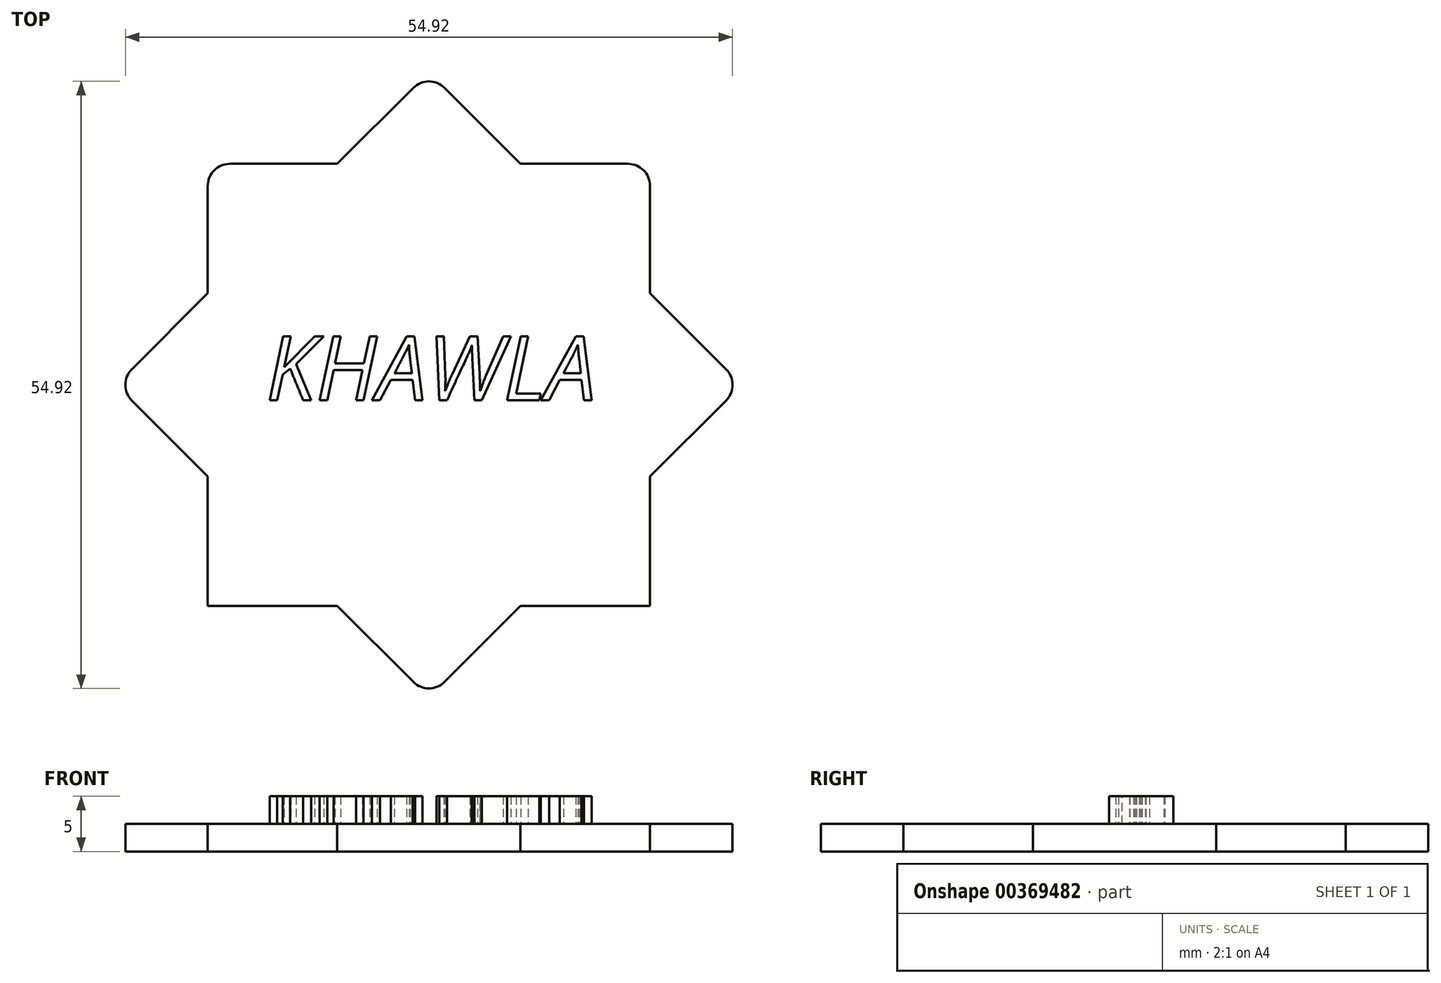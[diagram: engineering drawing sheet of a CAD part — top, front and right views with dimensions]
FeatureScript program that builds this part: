
annotation { "Feature Type Name" : "Feature", "Feature Type Description" : "" }
export const myFeature = defineFeature(function(context is Context, id is Id, definition is map)
    precondition{}
    {
        {
            var Q0;
            Q0=qCreatedBy(makeId("Top.planeOp"),FACE);
            var sketch = newSketch(context, id + "F0", { "sketchPlane" : qUnion([Q0])});
            skLineSegment(sketch, "E0.bottom", {"start": v(20, -20) * mm, "end": v(-20, -20) * mm});
            skLineSegment(sketch, "E0.top", {"start": v(18, 20) * mm, "end": v(-18, 20) * mm});
            skLineSegment(sketch, "E0.left", {"start": v(20, -20) * mm, "end": v(20, 18) * mm});
            skLineSegment(sketch, "E0.right", {"start": v(-20, -20) * mm, "end": v(-20, 18) * mm});
            skPoint(sketch, "E0.middle", {"position": v(0, 0) * mm});
            skCircle(sketch, "E1.cCircle", {"center": v(0, 0) * mm, "radius": 28.28 * mm, "construction": true});
            skLineSegment(sketch, "E1.0", {"start": v(26.87, -1.41) * mm, "end": v(1.41, -26.87) * mm});
            skLineSegment(sketch, "E1.1", {"start": v(-1.41, -26.87) * mm, "end": v(-26.87, -1.41) * mm});
            skLineSegment(sketch, "E1.2", {"start": v(-26.87, 1.41) * mm, "end": v(-1.41, 26.87) * mm});
            skLineSegment(sketch, "E1.3", {"start": v(1.41, 26.87) * mm, "end": v(26.87, 1.41) * mm});
            skPoint(sketch, "E2.visualSharp", {"position": v(0, 28.28) * mm});
            skArc(sketch, "E2.filletArc", {"start": v(1.41, 26.87) * mm, "mid": v(0, 27.46) * mm, "end": v(-1.41, 26.87) * mm});
            skPoint(sketch, "E3.visualSharp", {"position": v(28.28, 0) * mm});
            skArc(sketch, "E3.filletArc", {"start": v(26.87, -1.41) * mm, "mid": v(27.46, 0) * mm, "end": v(26.87, 1.41) * mm});
            skPoint(sketch, "E4.visualSharp", {"position": v(20, 20) * mm});
            skArc(sketch, "E4.filletArc", {"start": v(20, 18) * mm, "mid": v(19.41, 19.41) * mm, "end": v(18, 20) * mm});
            skPoint(sketch, "E5.visualSharp", {"position": v(-20, 20) * mm});
            skArc(sketch, "E5.filletArc", {"start": v(-18, 20) * mm, "mid": v(-19.41, 19.41) * mm, "end": v(-20, 18) * mm});
            skPoint(sketch, "E6.visualSharp", {"position": v(-28.28, 0) * mm});
            skArc(sketch, "E6.filletArc", {"start": v(-26.87, 1.41) * mm, "mid": v(-27.46, 0) * mm, "end": v(-26.87, -1.41) * mm});
            skPoint(sketch, "E7.visualSharp", {"position": v(0, -28.28) * mm});
            skArc(sketch, "E7.filletArc", {"start": v(-1.41, -26.87) * mm, "mid": v(0, -27.46) * mm, "end": v(1.41, -26.87) * mm});
            skSolve(sketch);
        }
        {
            var Q0;
            Q0 = qSketchRegion(id + "F0", true);
            extrude(context, id + "F1", {"entities" : qUnion([Q0]), "depth" : 2.5 * mm});
        }
        {
            var Q0;
            Q0=makeQuery(id+"F1.opExtrude","CAP_FACE",FACE,{"disambiguationData":[OSD([sQuery(id+"F0.wireOp",EDGE,"E0.bottom"),sQuery(id+"F0.wireOp",EDGE,"E0.top"),sQuery(id+"F0.wireOp",EDGE,"E0.left"),sQuery(id+"F0.wireOp",EDGE,"E0.right"),sQuery(id+"F0.wireOp",EDGE,"E1.0"),sQuery(id+"F0.wireOp",EDGE,"E1.1"),sQuery(id+"F0.wireOp",EDGE,"E1.2"),sQuery(id+"F0.wireOp",EDGE,"E1.3")])],"isStart":false});
            var sketch = newSketch(context, id + "F2", { "sketchPlane" : qUnion([Q0])});
            skSolve(sketch);
        }
        {
            var Q0;
            {var subQ3=sQuery(id+"F0.wireOp",EDGE,"E0.bottom");var subQ7=sQuery(id+"F0.wireOp",EDGE,"E0.left");var subQ18=makeQuery(id+"F0.imprint","INTERSECT",VERTEX,{"derivedFrom":[subQ3,subQ7]});Q0=makeQuery(id+"F2.imprint","IMPRINT",FACE,{"disambiguationData":[TD([[makeQuery(id+"F2.imprint","IMPRINT",EDGE,{"derivedFrom":makeQuery(id+"F1.opExtrude","CAP_EDGE",EDGE,{"disambiguationData":[OSD([subQ3]),TDD([makeQuery(id+"F0.imprint","IMPRINT",EDGE,{"disambiguationData":[TD([[subQ18,-1.0]])],"derivedFrom":subQ3})])],"isStart":false})}),-1.0]])]});}
            var sketch = newSketch(context, id + "F3", { "sketchPlane" : qUnion([Q0])});
            skText(sketch, "E8", { "text": "KHAWLA", "fontName": "OpenSans-Italic.ttf"});
            const initialGuessF3  = {"E8": [-0.01474, -0.0014, 1, 0, 0.00585]};
            skSetInitialGuess(sketch, initialGuessF3);
            skSolve(sketch);
        }
        {
            var Q0;
            Q0 = qSketchRegion(id + "F3", true);
            extrude(context, id + "F4", {"entities" : qUnion([Q0]), "operationType" : NewBodyOperationType.ADD, "depth" : 2.5 * mm});
        }
    });
